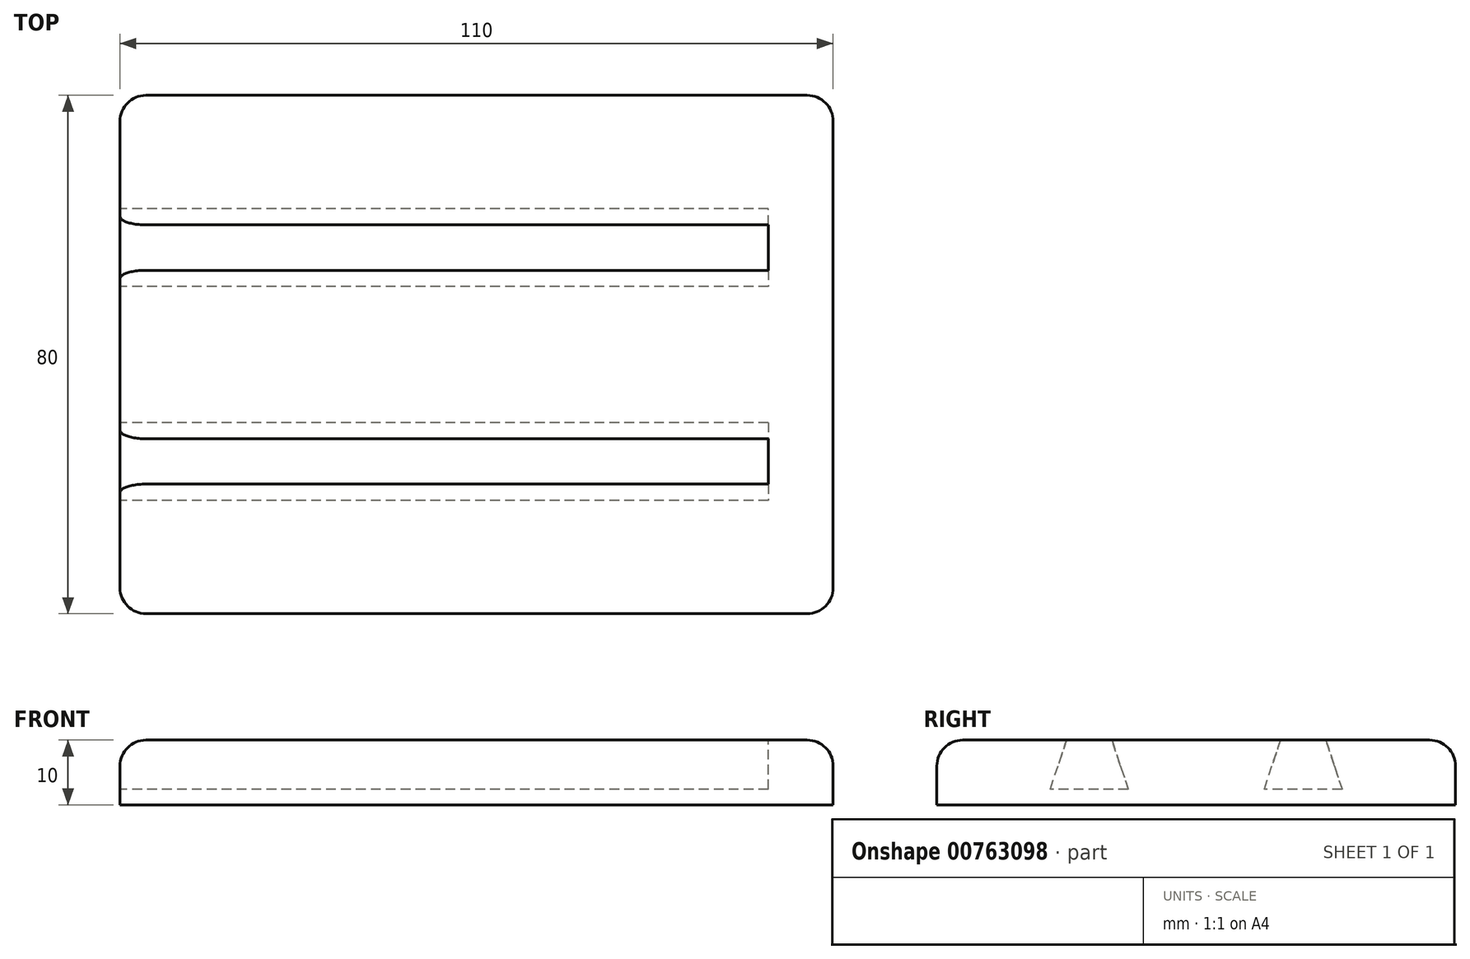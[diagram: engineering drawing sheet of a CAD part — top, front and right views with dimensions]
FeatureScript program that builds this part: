
annotation { "Feature Type Name" : "Feature", "Feature Type Description" : "" }
export const myFeature = defineFeature(function(context is Context, id is Id, definition is map)
    precondition{}
    {
        {
            var Q0;
            Q0=qCreatedBy(makeId("Top.planeOp"),FACE);
            var sketch = newSketch(context, id + "F0", { "sketchPlane" : qUnion([Q0])});
            skLineSegment(sketch, "E0.bottom", {"start": v(0, 0) * mm, "end": v(110, 0) * mm});
            skLineSegment(sketch, "E0.top", {"start": v(0, 80) * mm, "end": v(110, 80) * mm});
            skLineSegment(sketch, "E0.left", {"start": v(0, 0) * mm, "end": v(0, 80) * mm});
            skLineSegment(sketch, "E0.right", {"start": v(110, 0) * mm, "end": v(110, 80) * mm});
            skLineSegment(sketch, "E1.bottom", {"start": v(5, 75) * mm, "end": v(105, 75) * mm, "construction": true});
            skLineSegment(sketch, "E1.top", {"start": v(5, 5) * mm, "end": v(105, 5) * mm, "construction": true});
            skLineSegment(sketch, "E1.left", {"start": v(5, 75) * mm, "end": v(5, 5) * mm, "construction": true});
            skLineSegment(sketch, "E1.right", {"start": v(105, 75) * mm, "end": v(105, 5) * mm, "construction": true});
            skSolve(sketch);
        }
        {
            var Q0;
            Q0 = qSketchRegion(id + "F0", true);
            extrude(context, id + "F1", {"entities" : qUnion([Q0]), "depth" : 10 * mm, "offsetDistance" : 25 * mm});
        }
        {
            var Q0;
            Q0=makeQuery(id+"F1.opExtrude","SWEPT_FACE",FACE,{"disambiguationData":[OSD([sQuery(id+"F0.wireOp",EDGE,"E0.left")])]});
            var sketch = newSketch(context, id + "F2", { "sketchPlane" : qUnion([Q0])});
            skLineSegment(sketch, "E2", {"start": v(-80, 10) * mm, "end": v(-60, 10) * mm});
            skLineSegment(sketch, "E3", {"start": v(-60, 10) * mm, "end": v(-62.5, 17.6) * mm, "construction": true});
            skLineSegment(sketch, "E4", {"start": v(-62.5, 17.6) * mm, "end": v(-50.5, 17.6) * mm, "construction": true});
            skLineSegment(sketch, "E5", {"start": v(-50.5, 17.6) * mm, "end": v(-53, 10) * mm, "construction": true});
            skLineSegment(sketch, "E6", {"start": v(-27, 10) * mm, "end": v(-29.5, 17.6) * mm, "construction": true});
            skLineSegment(sketch, "E7", {"start": v(-29.5, 17.6) * mm, "end": v(-17.5, 17.6) * mm, "construction": true});
            skLineSegment(sketch, "E8", {"start": v(-17.5, 17.6) * mm, "end": v(-20, 10) * mm, "construction": true});
            skLineSegment(sketch, "E9.MirrorCS", {"start": v(-60, 10) * mm, "end": v(-62.5, 2.4) * mm});
            skLineSegment(sketch, "E10.MirrorCS", {"start": v(-62.5, 2.4) * mm, "end": v(-50.5, 2.4) * mm});
            skLineSegment(sketch, "E11.MirrorCS", {"start": v(-17.5, 2.4) * mm, "end": v(-20, 10) * mm});
            skLineSegment(sketch, "E12.MirrorCS", {"start": v(-50.5, 2.4) * mm, "end": v(-53, 10) * mm});
            skLineSegment(sketch, "E13.MirrorCS", {"start": v(-27, 10) * mm, "end": v(-29.5, 2.4) * mm});
            skLineSegment(sketch, "E14.MirrorCS", {"start": v(-29.5, 2.4) * mm, "end": v(-17.5, 2.4) * mm});
            skLineSegment(sketch, "E15", {"start": v(-40, 10) * mm, "end": v(0, 10) * mm, "construction": true});
            skSolve(sketch);
        }
        {
            var Q0;
            {var subQ0=sQuery(id+"F2.wireOp",EDGE,"E9.MirrorCS");Q0=makeQuery(id+"F2.imprint","IMPRINT",FACE,{"disambiguationData":[TD([[makeQuery(id+"F2.imprint","IMPRINT",EDGE,{"derivedFrom":subQ0}),1.0]])]});}
            var Q1;
            {var subQ0=sQuery(id+"F2.wireOp",EDGE,"E11.MirrorCS");Q1=makeQuery(id+"F2.imprint","IMPRINT",FACE,{"disambiguationData":[TD([[makeQuery(id+"F2.imprint","IMPRINT",EDGE,{"derivedFrom":subQ0}),1.0]])]});}
            extrude(context, id + "F3", {"entities" : qUnion([Q0, Q1]), "operationType" : NewBodyOperationType.REMOVE, "oppositeDirection" : true, "depth" : 100 * mm, "offsetDistance" : 25 * mm});
        }
        {
            var Q0;
            Q0=makeQuery(id+"F1.opExtrude","SWEPT_EDGE",EDGE,{"disambiguationData":[OSD([sQuery(id+"F0.wireOp",EDGE,"E0.bottom"),sQuery(id+"F0.wireOp",EDGE,"E0.left")])]});
            var Q1;
            Q1=makeQuery(id+"F1.opExtrude","SWEPT_EDGE",EDGE,{"disambiguationData":[OSD([sQuery(id+"F0.wireOp",EDGE,"E0.bottom"),sQuery(id+"F0.wireOp",EDGE,"E0.right")])]});
            var Q2;
            Q2=makeQuery(id+"F1.opExtrude","SWEPT_EDGE",EDGE,{"disambiguationData":[OSD([sQuery(id+"F0.wireOp",EDGE,"E0.top"),sQuery(id+"F0.wireOp",EDGE,"E0.right")])]});
            var Q3;
            Q3=makeQuery(id+"F1.opExtrude","SWEPT_EDGE",EDGE,{"disambiguationData":[OSD([sQuery(id+"F0.wireOp",EDGE,"E0.top"),sQuery(id+"F0.wireOp",EDGE,"E0.left")])]});
            var Q4;
            Q4=makeQuery(id+"F1.opExtrude","CAP_EDGE",EDGE,{"disambiguationData":[OSD([sQuery(id+"F0.wireOp",EDGE,"E0.top")])],"isStart":false});
            var Q5;
            Q5=makeQuery(id+"F1.opExtrude","CAP_EDGE",EDGE,{"disambiguationData":[OSD([sQuery(id+"F0.wireOp",EDGE,"E0.right")])],"isStart":false});
            var Q6;
            Q6=makeQuery(id+"F1.opExtrude","CAP_EDGE",EDGE,{"disambiguationData":[OSD([sQuery(id+"F0.wireOp",EDGE,"E0.bottom")])],"isStart":false});
            var Q7;
            {var subQ0=sQuery(id+"F0.wireOp",EDGE,"E0.bottom");var subQ1=sQuery(id+"F0.wireOp",EDGE,"E0.left");Q7=makeQuery(id+"F3.boolean.opBoolean","SPLIT",EDGE,{"disambiguationData":[TD([makeQuery(id+"F1.opExtrude","SWEPT_FACE",FACE,{"disambiguationData":[OSD([subQ0])]})])],"derivedFrom":makeQuery(id+"F1.opExtrude","CAP_EDGE",EDGE,{"disambiguationData":[OSD([subQ1])],"isStart":false})});}
            var Q8;
            {var subQ0=sQuery(id+"F0.wireOp",EDGE,"E0.left");Q8=makeQuery(id+"F3.boolean.opBoolean","SPLIT",EDGE,{"disambiguationData":[TD([makeQuery(id+"F3.opExtrude","SWEPT_FACE",FACE,{"disambiguationData":[OSD([sQuery(id+"F2.wireOp",EDGE,"E12.MirrorCS")])]})])],"derivedFrom":makeQuery(id+"F1.opExtrude","CAP_EDGE",EDGE,{"disambiguationData":[OSD([subQ0])],"isStart":false})});}
            var Q9;
            {var subQ0=sQuery(id+"F0.wireOp",EDGE,"E0.left");var subQ1=sQuery(id+"F0.wireOp",EDGE,"E0.top");Q9=makeQuery(id+"F3.boolean.opBoolean","SPLIT",EDGE,{"disambiguationData":[TD([makeQuery(id+"F1.opExtrude","SWEPT_FACE",FACE,{"disambiguationData":[OSD([subQ1])]})])],"derivedFrom":makeQuery(id+"F1.opExtrude","CAP_EDGE",EDGE,{"disambiguationData":[OSD([subQ0])],"isStart":false})});}
            fillet(context, id + "F4", {"entities" : qUnion([Q0, Q1, Q2, Q3, Q4, Q5, Q6, Q7, Q8, Q9]), "radius" : 4 * mm, "tangentPropagation" : true, "allowEdgeOverflow" : false});
        }
    });
